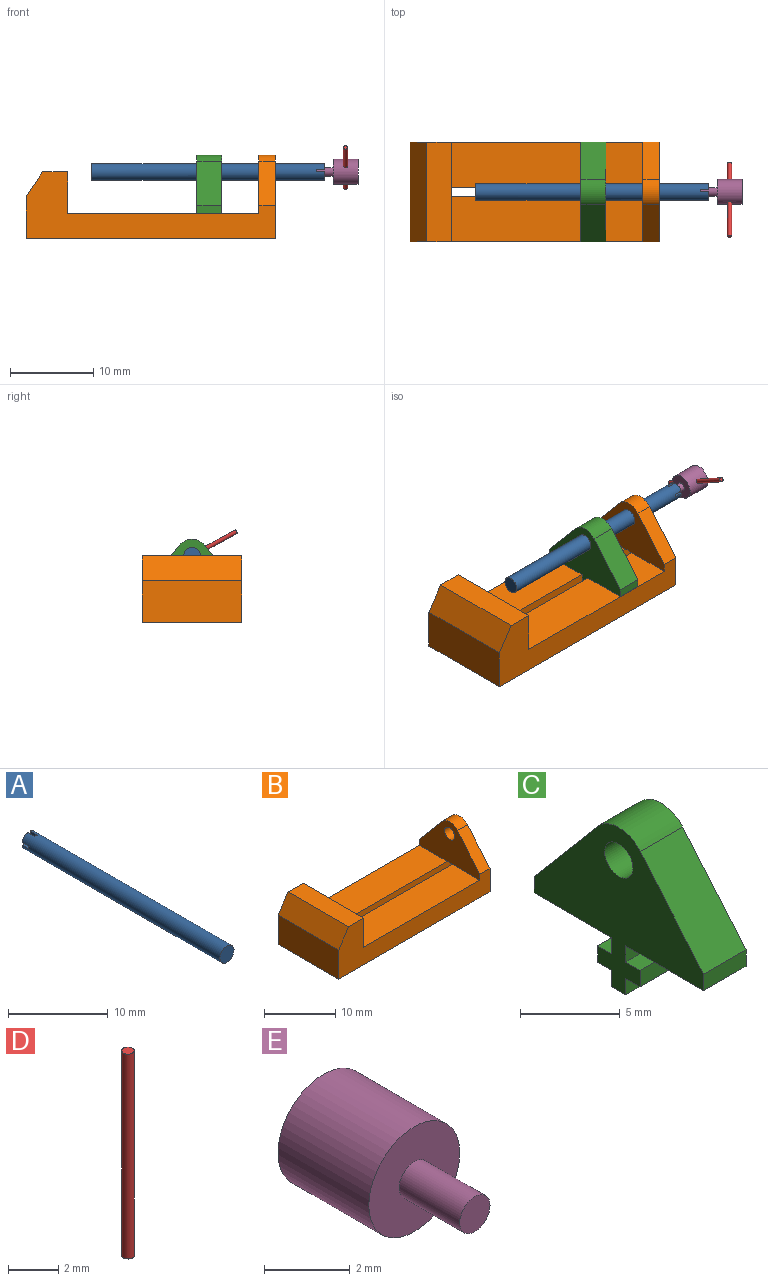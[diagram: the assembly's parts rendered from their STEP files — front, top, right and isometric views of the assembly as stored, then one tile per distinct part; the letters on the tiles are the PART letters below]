
ASSEMBLY  parts=5 mates=6
PART A: 19 faces, bbox 2x28x2 mm
  f0: cylinder r=1mm len=28mm, axis (0,1,0), area 174.7mm2, adj f1,f2,f3,f4,f5,f6,f7,f8
  f1: plane 0.84x0.84mm, normal (0,1,0), area 0.4mm2, adj f0,f10,f11,f16
  f2: plane 0.84x0.84mm, normal (0,1,0), area 0.4mm2, adj f0,f12,f13,f17
  f3: plane 0.84x0.84mm, normal (0,1,0), area 0.4mm2, adj f0,f7,f14,f18
  f4: plane 2x2mm, normal (0,-1,0), area 3.1mm2, adj f0
  f5: plane 0.84x0.84mm, normal (0,1,0), area 0.4mm2, adj f0,f8,f9,f15
  f6: plane 2x2mm, normal (0,1,0), area 1.4mm2, adj f0,f7,f8,f9,f10,f11,f12,f13
  f7: plane 1x0.51mm, normal (0,0,-1), area 0.5mm2, adj f0,f3,f6,f18
  f8: plane 1x0.51mm, normal (0,0,1), area 0.5mm2, adj f0,f5,f6,f15
  f9: plane 1x0.51mm, normal (-1,0,0), area 0.5mm2, adj f0,f5,f6,f15
  f10: plane 1x0.51mm, normal (1,0,0), area 0.5mm2, adj f0,f1,f6,f16
  f11: plane 1x0.51mm, normal (0,0,1), area 0.5mm2, adj f0,f1,f6,f16
  f12: plane 1x0.51mm, normal (0,0,-1), area 0.5mm2, adj f0,f2,f6,f17
  f13: plane 1x0.51mm, normal (1,0,0), area 0.5mm2, adj f0,f2,f6,f17
  f14: plane 1x0.51mm, normal (-1,0,0), area 0.5mm2, adj f0,f3,f6,f18
  f15: cylinder r=0.5mm len=1mm, axis (0,1,0), area 0.5mm2, adj f5,f6,f8,f9
  f16: cylinder r=0.5mm len=1mm, axis (0,1,0), area 0.5mm2, adj f1,f6,f10,f11
  f17: cylinder r=0.5mm len=1mm, axis (0,1,0), area 0.5mm2, adj f2,f6,f12,f13
  f18: cylinder r=0.5mm len=1mm, axis (0,1,0), area 0.5mm2, adj f3,f6,f7,f14
PART B: 26 faces, bbox 30x12x10 mm
  f0: plane 12x5mm, normal (-1,0,0), area 60mm2, adj f4,f5,f8,f9
  f1: plane 23x5.5mm, normal (0,0,1), area 126.5mm2, adj f6,f9,f14,f24
  f2: plane 12x10mm, normal (1,0,0), area 81.2mm2, adj f5,f8,f9,f10,f11,f12,f13,f15
  f3: plane 23x5.5mm, normal (0,0,1), area 126.5mm2, adj f6,f8,f14,f15
  f4: plane 12x3mm, normal (-0.83,0,0.55), area 43.3mm2, adj f0,f7,f8,f9
  f5: plane 30x12mm, normal (0,0,-1), area 335mm2, adj f0,f2,f6,f8,f9,f19,f20
  f6: plane 12x8mm, normal (1,0,0), area 65mm2, adj f1,f3,f5,f7,f8,f9,f15,f16
  f7: plane 12x3mm, normal (0,0,1), area 36mm2, adj f4,f6,f8,f9
  f8: plane 30x8mm, normal (0,-1,0), area 114mm2, adj f0,f2,f3,f4,f5,f6,f7,f12
  f9: plane 30x8mm, normal (0,1,0), area 114mm2, adj f0,f1,f2,f4,f5,f6,f7,f10
  f10: plane 5.29x4.47mm, normal (0,0.76,0.65), area 13.9mm2, adj f2,f9,f11,f14
  f11: cylinder r=2mm len=3.06mm, axis (1,0,0), area 7mm2, adj f2,f10,f12,f14
  f12: plane 5.29x4.47mm, normal (0,-0.76,0.65), area 13.9mm2, adj f2,f8,f11,f14
  f13: cylinder r=1mm len=2mm, axis (1,0,0), area 12.6mm2, adj f2,f14
  f14: plane 12x7mm, normal (-1,0,0), area 50.2mm2, adj f1,f3,f8,f9,f10,f11,f12,f13
  f15: plane 25x1mm, normal (0,1,0), area 25mm2, adj f2,f3,f6,f16,f25
  f16: plane 25x1mm, normal (0,0,-1), area 25mm2, adj f2,f6,f15,f17
  f17: plane 25x1mm, normal (0,1,0), area 25mm2, adj f2,f6,f16,f18
  f18: plane 25x1mm, normal (0,0,1), area 25mm2, adj f2,f6,f17,f19
  f19: plane 25x1mm, normal (0,1,0), area 25mm2, adj f2,f5,f6,f18
  f20: plane 25x1mm, normal (0,-1,0), area 25mm2, adj f2,f5,f6,f21
  f21: plane 25x1mm, normal (0,0,1), area 25mm2, adj f2,f6,f20,f22
  f22: plane 25x1mm, normal (0,-1,0), area 25mm2, adj f2,f6,f21,f23
  f23: plane 25x1mm, normal (0,0,-1), area 25mm2, adj f2,f6,f22,f24
  f24: plane 25x1mm, normal (0,-1,0), area 25mm2, adj f1,f2,f6,f23,f25
  f25: plane 2x1mm, normal (0,0,-1), area 2mm2, adj f2,f14,f15,f24
PART C: 21 faces, bbox 3x12x10 mm
  f0: plane 12x10mm, normal (-1,0,0), area 55.2mm2, adj f1,f2,f4,f5,f6,f7,f8,f9
  f1: cylinder r=2mm len=3.06mm, axis (1,0,0), area 10.4mm2, adj f0,f3,f4,f5
  f2: cylinder r=1mm len=3mm, axis (1,0,0), area 18.8mm2, adj f0,f3
  f3: plane 12x10mm, normal (1,0,0), area 55.2mm2, adj f1,f2,f4,f5,f6,f7,f8,f9
  f4: plane 5.29x4.47mm, normal (0,-0.76,0.65), area 20.8mm2, adj f0,f1,f3,f19
  f5: plane 5.29x4.47mm, normal (0,0.76,0.65), area 20.8mm2, adj f0,f1,f3,f12
  f6: plane 5.5x3mm, normal (0,0,-1), area 16.5mm2, adj f0,f3,f7,f12
  f7: plane 3x1mm, normal (0,1,0), area 3mm2, adj f0,f3,f6,f8
  f8: plane 3x1mm, normal (0,0,1), area 3mm2, adj f0,f3,f7,f9
  f9: plane 3x1mm, normal (0,1,0), area 3mm2, adj f0,f3,f8,f10
  f10: plane 3x1mm, normal (0,0,-1), area 3mm2, adj f0,f3,f9,f11
  f11: plane 3x1mm, normal (0,1,0), area 3mm2, adj f0,f3,f10,f20
  f12: plane 3x1mm, normal (0,1,0), area 3mm2, adj f0,f3,f5,f6
  f13: plane 3x1mm, normal (0,-1,0), area 3mm2, adj f0,f3,f14,f20
  f14: plane 3x1mm, normal (0,0,-1), area 3mm2, adj f0,f3,f13,f15
  f15: plane 3x1mm, normal (0,-1,0), area 3mm2, adj f0,f3,f14,f16
  f16: plane 3x1mm, normal (0,0,1), area 3mm2, adj f0,f3,f15,f18
  f17: plane 5.5x3mm, normal (0,0,-1), area 16.5mm2, adj f0,f3,f18,f19
  f18: plane 3x1mm, normal (0,-1,0), area 3mm2, adj f0,f3,f16,f17
  f19: plane 3x1mm, normal (0,-1,0), area 3mm2, adj f0,f3,f4,f17
  f20: plane 3x1mm, normal (0,0,-1), area 3mm2, adj f0,f3,f11,f13
PART D: 3 faces, bbox 0.5x0.5x10 mm
  f0: cylinder r=0.25mm len=10mm, axis (0,0,-1), area 15.7mm2, adj f1,f2
  f1: plane 0.5x0.5mm, normal (0,0,1), area 0.2mm2, adj f0
  f2: plane 0.5x0.5mm, normal (0,0,-1), area 0.2mm2, adj f0
PART E: 7 faces, bbox 3x5x3 mm
  f0: cylinder r=0.5mm len=2mm, axis (0,1,0), area 6.3mm2, adj f1,f3
  f1: plane 1x1mm, normal (0,-1,0), area 0.8mm2, adj f0
  f2: cylinder r=1.5mm len=3mm, axis (0,1,0), area 28.1mm2, adj f3,f4,f5
  f3: plane 3x3mm, normal (0,-1,0), area 6.3mm2, adj f0,f2
  f4: plane 3x3mm, normal (0,1,0), area 7.1mm2, adj f2
  f5: cylinder r=0.25mm len=0.84mm, axis (1,0,0), area 1.3mm2, adj f2,f6
  f6: plane 0.5x0.5mm, normal (1,0,0), area 0.2mm2, adj f5
PLACE A rot(axis=(0.54,0.54,-0.65),114.2deg) t=(19.91,34.11,-11.32)mm
PLACE B t=(-13.01,4.85,-2.46)mm fixed
PLACE C t=(10.53,4.85,-2.46)mm
PLACE D rot(axis=(-0.97,0.21,0.12),120.4deg) t=(92.96,10.1,23.18)mm
PLACE E rot(axis=(-0.24,-0.24,-0.94),93.6deg) t=(26.91,-6.21,44.49)mm
MATE planar C.f16 <-> B.f16  axis (0,0,1) through (10.53,-2.15,-5.46)mm
MATE planar C.f13 <-> B.f19  axis (0,-1,0) through (9.03,-1.65,-6.96)mm
MATE planar E.f0 <-> A.f6  axis (-1,0,0) through (21.91,-1.15,0.54)mm
MATE cylindrical A.f0 <-> C.f1  axis (1,0,0) through (8.91,-1.15,0.54)mm
MATE cylindrical E.f0 <-> A.f0  axis (-1,0,0) through (21.91,-1.15,0.54)mm
MATE revolute D.f0 <-> E.f5  axis (0,-0.88,0.48) through (25.41,-2.1,1.07)mm
